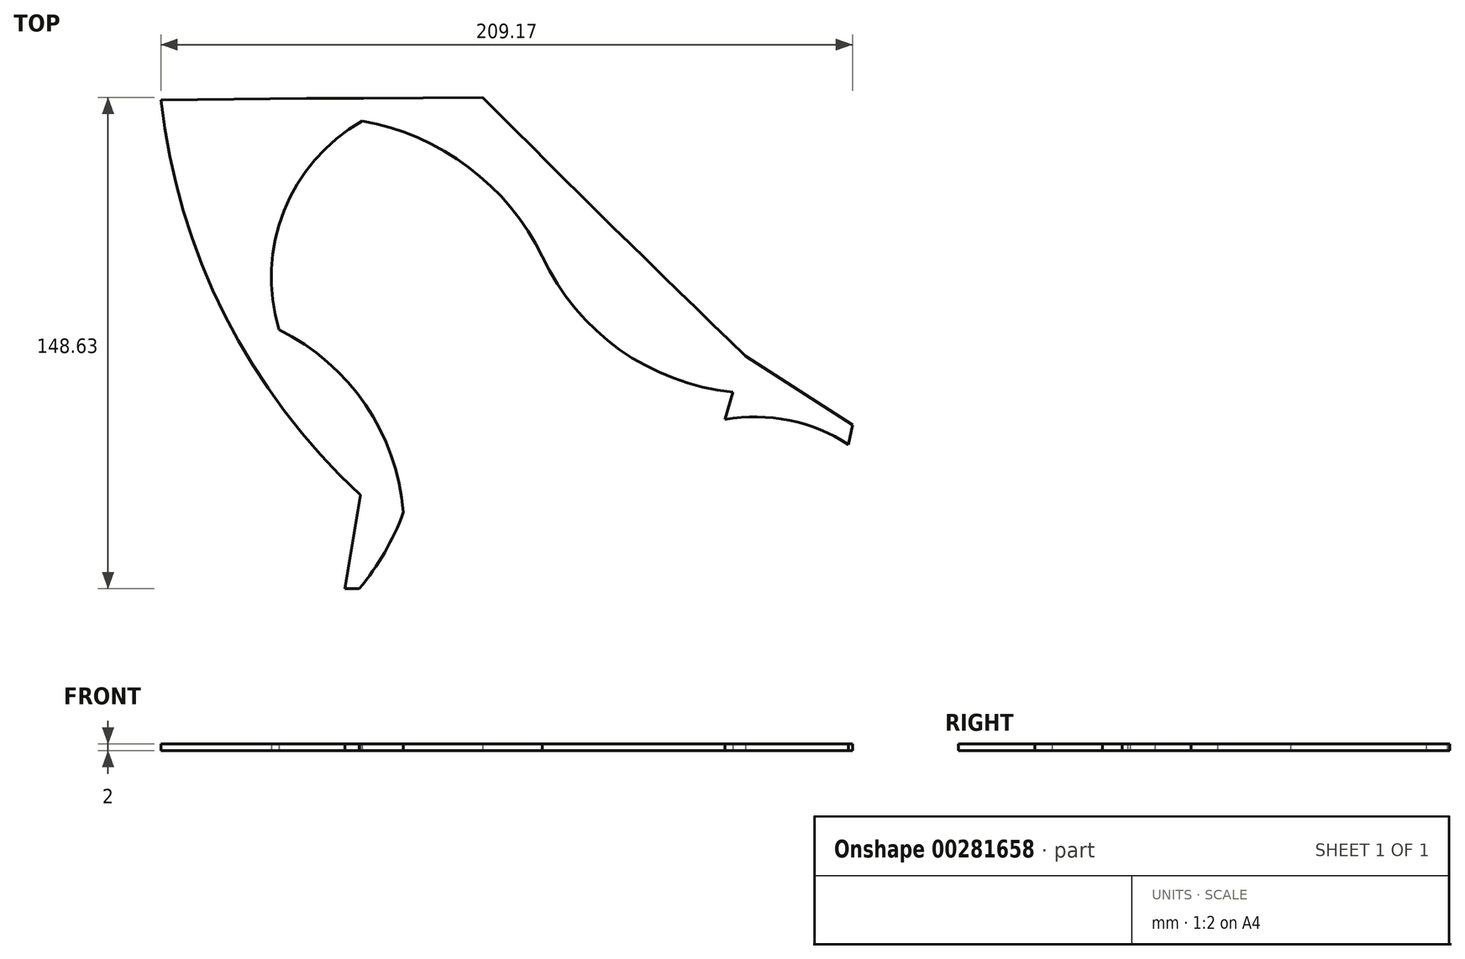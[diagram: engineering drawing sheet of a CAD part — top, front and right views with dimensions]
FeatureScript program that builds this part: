
annotation { "Feature Type Name" : "Feature", "Feature Type Description" : "" }
export const myFeature = defineFeature(function(context is Context, id is Id, definition is map)
    precondition{}
    {
        {
            var Q0;
            Q0=qCreatedBy(makeId("Top.planeOp"),FACE);
            var sketch = newSketch(context, id + "F0", { "sketchPlane" : qUnion([Q0])});
            skLineSegment(sketch, "E0", {"start": v(-13.35, 0) * mm, "end": v(-17.72, 0) * mm});
            skLineSegment(sketch, "E1", {"start": v(-17.72, 0) * mm, "end": v(-12.95, 28.3) * mm});
            skLineSegment(sketch, "E2", {"start": v(-29.24, 148.3) * mm, "end": v(-73.35, 147.9) * mm});
            skLineSegment(sketch, "E3", {"start": v(-12.16, 148.3) * mm, "end": v(24.01, 148.63) * mm});
            skLineSegment(sketch, "E4", {"start": v(99.66, 59.5) * mm, "end": v(97.27, 51.16) * mm});
            skLineSegment(sketch, "E5", {"start": v(134.62, 43.61) * mm, "end": v(135.82, 49.57) * mm});
            skLineSegment(sketch, "E6", {"start": v(135.82, 49.57) * mm, "end": v(103.47, 70.42) * mm});
            skLineSegment(sketch, "E7", {"start": v(-12.16, 148.3) * mm, "end": v(-29.24, 148.3) * mm});
            skArc(sketch, "E8", {"start": v(42.04, 100.43) * mm, "mid": v(19.7, 127.53) * mm, "end": v(-12.55, 141.46) * mm});
            skArc(sketch, "E9", {"start": v(-12.55, 141.46) * mm, "mid": v(-36.13, 114.3) * mm, "end": v(-37.59, 78.37) * mm});
            skArc(sketch, "E10", {"start": v(0, 23.13) * mm, "mid": v(-11.52, 55.7) * mm, "end": v(-37.59, 78.37) * mm});
            skArc(sketch, "E11", {"start": v(42.04, 100.43) * mm, "mid": v(65.42, 72.33) * mm, "end": v(99.66, 59.5) * mm});
            skArc(sketch, "E12", {"start": v(24.01, 148.63) * mm, "mid": v(63.5, 109.29) * mm, "end": v(103.47, 70.42) * mm});
            skArc(sketch, "E13", {"start": v(-73.35, 147.9) * mm, "mid": v(-53.98, 82.64) * mm, "end": v(-12.95, 28.3) * mm});
            skArc(sketch, "E14", {"start": v(-13.35, 0) * mm, "mid": v(-5.68, 11) * mm, "end": v(0, 23.13) * mm});
            skArc(sketch, "E15", {"start": v(134.62, 43.61) * mm, "mid": v(116.67, 50.94) * mm, "end": v(97.27, 51.16) * mm});
            skSolve(sketch);
        }
        {
            var Q0;
            Q0=makeQuery(id+"F0.imprint","IMPRINT",FACE,{"disambiguationData":[TD([[makeQuery(id+"F0.imprint","IMPRINT",EDGE,{"derivedFrom":sQuery(id+"F0.wireOp",EDGE,"nIYb5HoD-kha2-nX5I-hkTI-P3YOmPk7qzv5")}),-1.0]])]});
            var Q1;
            Q1=makeQuery(id+"F0.imprint","IMPRINT",FACE,{"disambiguationData":[TD([[makeQuery(id+"F0.imprint","IMPRINT",EDGE,{"derivedFrom":sQuery(id+"F0.wireOp",EDGE,"E3")}),-1.0]])]});
            extrude(context, id + "F1", {"entities" : qUnion([Q0, Q1]), "depth" : 2 * mm});
        }
    });
